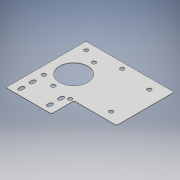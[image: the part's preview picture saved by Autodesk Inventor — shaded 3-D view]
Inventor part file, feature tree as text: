
AUTODESK INVENTOR PART (.ipt)
format: ipt  version: 2018 (Build 220112000, 112)  size: 157,696 bytes
history: native  units: mm
features: other x1, extrude x1, fillet x1, sketch x1
ambient origin geometry x8: Origin, YZ Plane, XZ Plane, XY Plane, X Axis, Y Axis, Z Axis, Center Point
bodies: Body1 (feature_tree)
feature tree (4):
  other  "Sólido1"
  extrude  "Extrusión1"  Depth=3.0mm
  fillet  "Empalme1"  Radius=9.0mm
  sketch  "Boceto1"  dims[d6=9.0mm d8=9.0mm d13=9.0mm d14=9.0mm d18=9.0mm d19=9.0mm d22=9.0mm d24=9.0mm d26=63.51mm d50=0.8mm d51=0.0mm d52=3.0mm]
